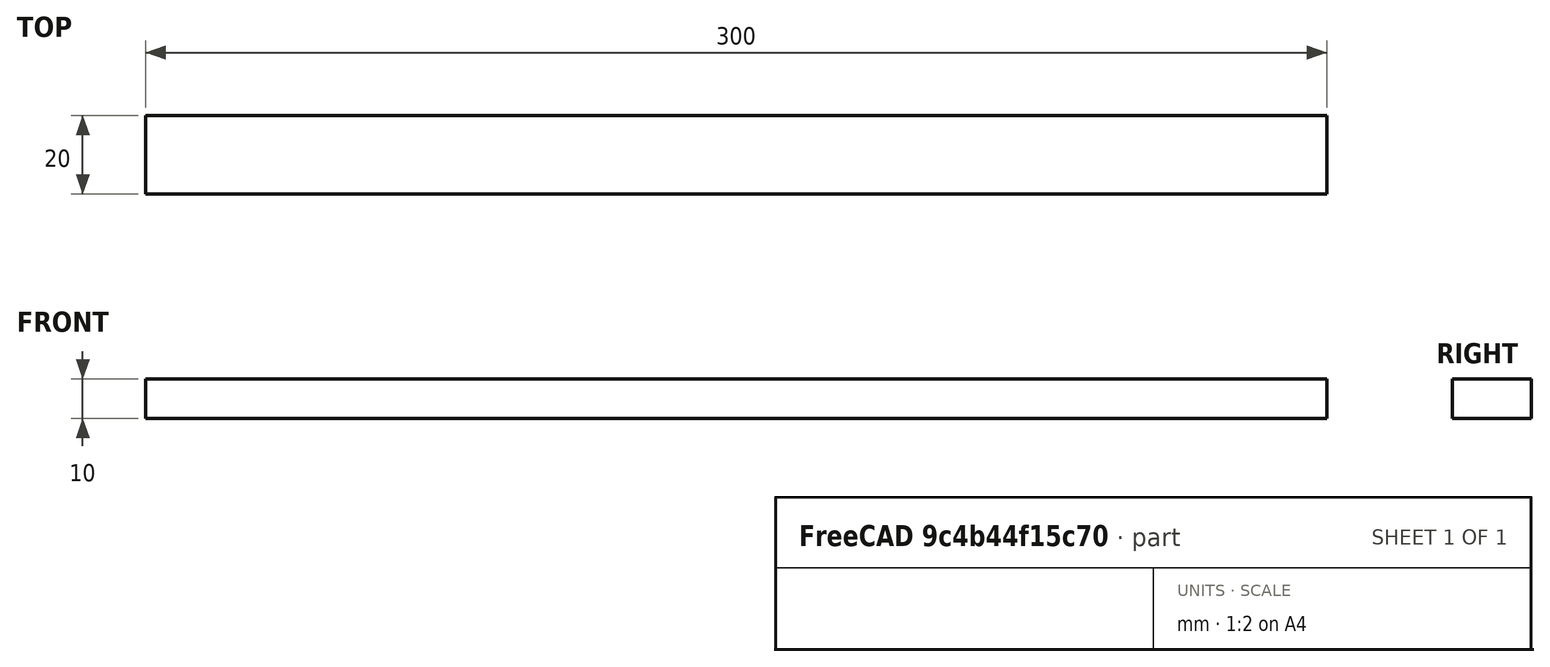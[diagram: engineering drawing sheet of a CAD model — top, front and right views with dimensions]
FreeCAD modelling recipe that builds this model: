
FCSTD DOCUMENT  (FreeCAD 0.20R29410 (Git))
Label: Bar_0mm
License: All rights reserved
LicenseURL: http://en.wikipedia.org/wiki/All_rights_reserved
objects: Sketcher::SketchObject×1, PartDesign::Pad×1, PartDesign::Body×1
note: 4 computed .brp shape members not serialized (recipe doc carries the construction recipe); baked Part::Feature solids carry a one-line shape summary decoded from their .brp

FEATURE [Sketcher::SketchObject] Sketch
  FullyConstrained = true
  MapMode = 5
  Placement = pos=(0,0,0) rot=(0.57735,0.57735,0.57735;2.0944rad)
  Support = -> [YZ_Plane]
  sketch-geometry (5):
    g0: LineSegment StartX=10 StartY=5 StartZ=0 EndX=10 EndY=-5 EndZ=0
    g1: LineSegment StartX=10 StartY=-5 StartZ=0 EndX=-10 EndY=-5 EndZ=0
    g2: LineSegment StartX=-10 StartY=-5 StartZ=0 EndX=-10 EndY=5 EndZ=0
    g3: LineSegment StartX=-10 StartY=5 StartZ=0 EndX=10 EndY=5 EndZ=0
    g4: GeomPoint X=1e-16 Y=1e-16 Z=0
  constraints (13):
    c: Coincident(g0,g1)
    c: Coincident(g1,g2)
    c: Coincident(g2,g3)
    c: Coincident(g3,g0)
    c: Horizontal(g1)
    c: Horizontal(g3)
    c: Vertical(g0)
    c: Vertical(g2)
    c: Symmetric(g1,g0,g4)
    c: DistanceY(g-1,g4) = 0
    c: DistanceX(g4,g-1) = 0
    c: DistanceX(g1,g1) = 20
    c: DistanceY(g2,g2) = 10
FEATURE [PartDesign::Pad] Pad
  Direction = (1,-2e-16,3e-16)
  Length = 300
  Length2 = 10
  Placement = pos=(0,0,0) rot=(0.57735,0.57735,0.57735;2.0944rad)
  Profile = -> Sketch
  ReferenceAxis = -> Sketch [N_Axis]
  Type = 0
FEATURE [PartDesign::Body] Body
  Group = -> [Sketch,Pad]
  Origin = -> Origin
  Tip = -> Pad
